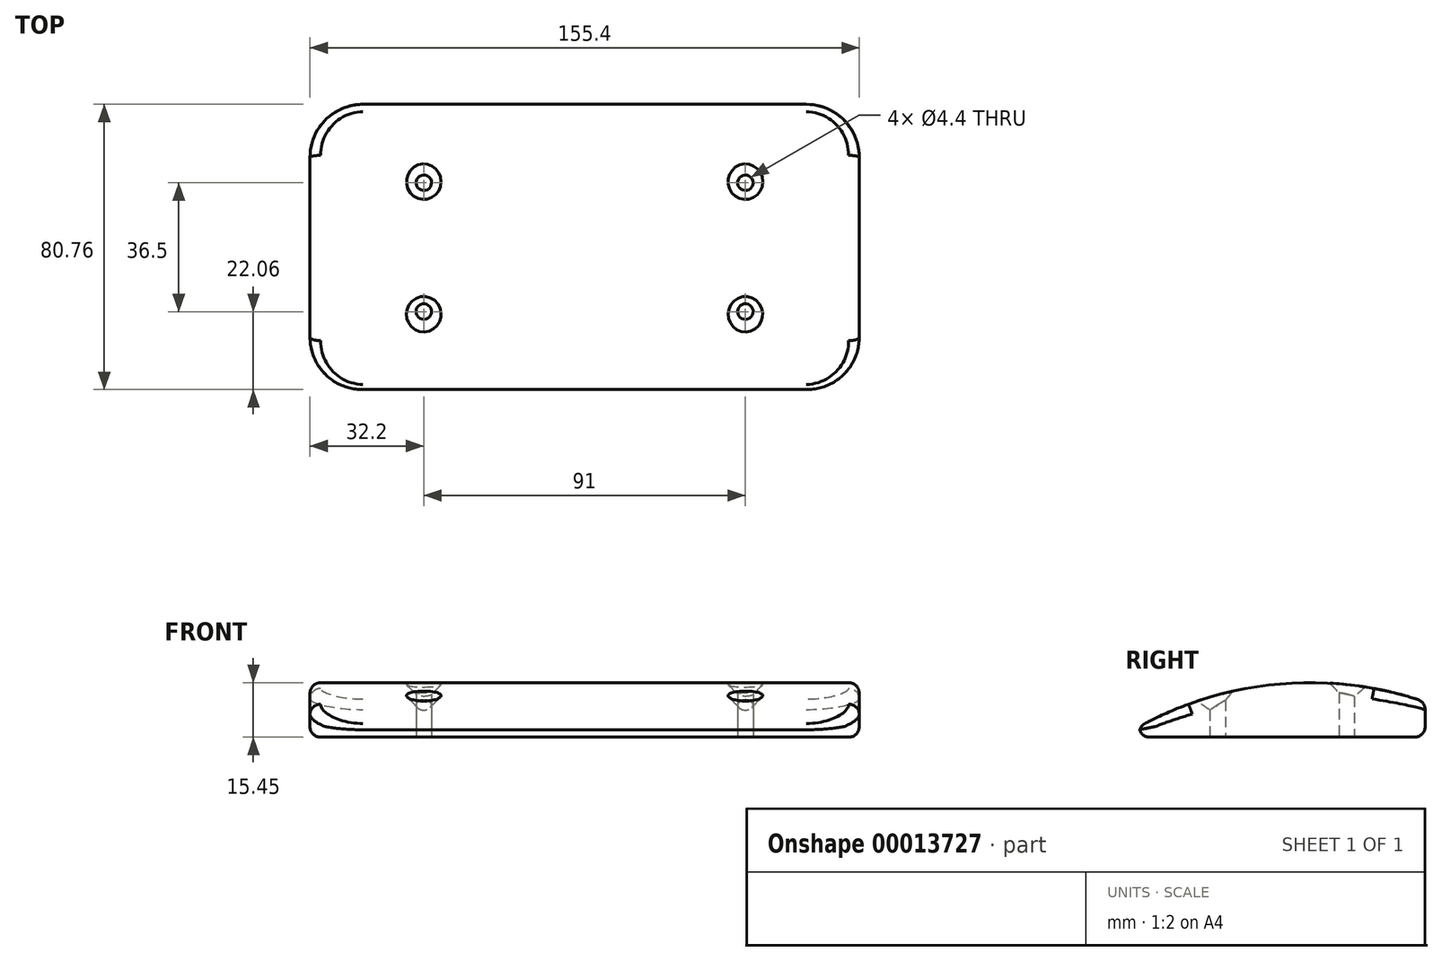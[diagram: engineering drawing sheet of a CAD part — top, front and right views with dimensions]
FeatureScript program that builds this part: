
annotation { "Feature Type Name" : "Feature", "Feature Type Description" : "" }
export const myFeature = defineFeature(function(context is Context, id is Id, definition is map)
    precondition{}
    {
        {
            var Q0;
            Q0=qCreatedBy(makeId("Top.planeOp"),FACE);
            var sketch = newSketch(context, id + "F0", { "sketchPlane" : qUnion([Q0])});
            skLineSegment(sketch, "E0", {"start": v(-45.5, 0) * mm, "end": v(45.5, 0) * mm, "construction": true});
            skLineSegment(sketch, "E1", {"start": v(45.5, 18.25) * mm, "end": v(45.5, -18.25) * mm, "construction": true});
            skLineSegment(sketch, "E2", {"start": v(-45.5, -18.25) * mm, "end": v(-45.5, 18.25) * mm, "construction": true});
            skCircle(sketch, "E3", {"center": v(-45.5, 18.25) * mm, "radius": 2.2 * mm});
            skCircle(sketch, "E4", {"center": v(-45.5, -18.25) * mm, "radius": 2.2 * mm});
            skCircle(sketch, "E5", {"center": v(45.5, -18.25) * mm, "radius": 2.2 * mm});
            skCircle(sketch, "E6", {"center": v(45.5, 18.25) * mm, "radius": 2.2 * mm});
            skLineSegment(sketch, "E7.rect.bottom", {"start": v(-77.7, 40.45) * mm, "end": v(77.7, 40.45) * mm});
            skLineSegment(sketch, "E7.rect.top", {"start": v(-77.7, -40.45) * mm, "end": v(77.7, -40.45) * mm});
            skLineSegment(sketch, "E7.rect.left", {"start": v(-77.7, 40.45) * mm, "end": v(-77.7, -40.45) * mm});
            skLineSegment(sketch, "E7.rect.right", {"start": v(77.7, 40.45) * mm, "end": v(77.7, -40.45) * mm});
            skPoint(sketch, "E7.rect.middle", {"position": v(0, 0) * mm});
            skPoint(sketch, "E8.visualSharp", {"position": v(-77.7, 40.45) * mm});
            skPoint(sketch, "E9.visualSharp", {"position": v(-77.7, -40.45) * mm});
            skPoint(sketch, "E10.visualSharp", {"position": v(77.7, -40.45) * mm});
            skPoint(sketch, "E11.visualSharp", {"position": v(77.7, 40.45) * mm});
            skSolve(sketch);
        }
        {
            var Q0;
            Q0=sQuery(id+"F0.wireOp",EDGE,"E7.rect.left");
            cPlane(context, id + "F1", {"entities" : qUnion([Q0]), "cplaneType" : CPlaneType.LINE_ANGLE, "offset" : 150 * mm, "angle" : 90 * degree, "width" : 150 * mm, "height" : 150 * mm});
        }
        {
            var Q0;
            Q0=qCreatedBy(id+"F1.planeOp",FACE);
            var sketch = newSketch(context, id + "F2", { "sketchPlane" : qUnion([Q0])});
            skLineSegment(sketch, "E12.0", {"start": v(40.45, 0) * mm, "end": v(-40.45, 0) * mm});
            skLineSegment(sketch, "E13", {"start": v(-40.45, 0) * mm, "end": v(-40.45, 3) * mm});
            skLineSegment(sketch, "E14", {"start": v(40.45, 10) * mm, "end": v(40.45, 0) * mm});
            skArc(sketch, "E15", {"start": v(40.45, 10) * mm, "mid": v(-0.74, 15.08) * mm, "end": v(-40.45, 3) * mm});
            skSolve(sketch);
        }
        {
            var Q0;
            Q0=sQuery(id+"F0.wireOp",EDGE,"E7.rect.right");
            cPlane(context, id + "F3", {"entities" : qUnion([Q0]), "cplaneType" : CPlaneType.LINE_ANGLE, "offset" : 150 * mm, "angle" : 90 * degree, "width" : 150 * mm, "height" : 150 * mm});
        }
        {
            var Q0;
            Q0=makeQuery(id+"F2.imprint","IMPRINT",FACE,{"disambiguationData":[TD([[makeQuery(id+"F2.imprint","IMPRINT",EDGE,{"derivedFrom":sQuery(id+"F2.wireOp",EDGE,"E12.0")}),-1.0]])]});
            var Q1;
            Q1=qCreatedBy(id+"F3.planeOp",FACE);
            extrude(context, id + "F4", {"entities" : qUnion([Q0]), "endBound" : BoundingType.UP_TO_SURFACE, "endBoundEntityFace" : qUnion([Q1]), "depth" : 25 * mm});
        }
        {
            var Q0;
            Q0=makeQuery(id+"F0.imprint","IMPRINT",FACE,{"disambiguationData":[TD([[makeQuery(id+"F0.imprint","IMPRINT",EDGE,{"derivedFrom":sQuery(id+"F0.wireOp",EDGE,"E4")}),1.0]])]});
            var Q1;
            Q1=makeQuery(id+"F0.imprint","IMPRINT",FACE,{"disambiguationData":[TD([[makeQuery(id+"F0.imprint","IMPRINT",EDGE,{"derivedFrom":sQuery(id+"F0.wireOp",EDGE,"E3")}),1.0]])]});
            var Q2;
            Q2=makeQuery(id+"F0.imprint","IMPRINT",FACE,{"disambiguationData":[TD([[makeQuery(id+"F0.imprint","IMPRINT",EDGE,{"derivedFrom":sQuery(id+"F0.wireOp",EDGE,"E5")}),1.0]])]});
            var Q3;
            Q3=makeQuery(id+"F0.imprint","IMPRINT",FACE,{"disambiguationData":[TD([[makeQuery(id+"F0.imprint","IMPRINT",EDGE,{"derivedFrom":sQuery(id+"F0.wireOp",EDGE,"E6")}),1.0]])]});
            extrude(context, id + "F5", {"entities" : qUnion([Q0, Q1, Q2, Q3]), "operationType" : NewBodyOperationType.REMOVE, "depth" : 25 * mm});
        }
        {
            var Q0;
            Q0=makeQuery(id+"F5.boolean.opBoolean","INTERSECT",EDGE,{"derivedFrom":[makeQuery(id+"F4.opExtrude","SWEPT_FACE",FACE,{"disambiguationData":[OSD([sQuery(id+"F2.wireOp",EDGE,"E15")])]}),makeQuery(id+"F5.opExtrude","SWEPT_FACE",FACE,{"disambiguationData":[OSD([sQuery(id+"F0.wireOp",EDGE,"E3")])]})]});
            var Q1;
            Q1=makeQuery(id+"F5.boolean.opBoolean","INTERSECT",EDGE,{"derivedFrom":[makeQuery(id+"F4.opExtrude","SWEPT_FACE",FACE,{"disambiguationData":[OSD([sQuery(id+"F2.wireOp",EDGE,"E15")])]}),makeQuery(id+"F5.opExtrude","SWEPT_FACE",FACE,{"disambiguationData":[OSD([sQuery(id+"F0.wireOp",EDGE,"E4")])]})]});
            var Q2;
            Q2=makeQuery(id+"F5.boolean.opBoolean","INTERSECT",EDGE,{"derivedFrom":[makeQuery(id+"F4.opExtrude","SWEPT_FACE",FACE,{"disambiguationData":[OSD([sQuery(id+"F2.wireOp",EDGE,"E15")])]}),makeQuery(id+"F5.opExtrude","SWEPT_FACE",FACE,{"disambiguationData":[OSD([sQuery(id+"F0.wireOp",EDGE,"E5")])]})]});
            var Q3;
            Q3=makeQuery(id+"F5.boolean.opBoolean","INTERSECT",EDGE,{"derivedFrom":[makeQuery(id+"F4.opExtrude","SWEPT_FACE",FACE,{"disambiguationData":[OSD([sQuery(id+"F2.wireOp",EDGE,"E15")])]}),makeQuery(id+"F5.opExtrude","SWEPT_FACE",FACE,{"disambiguationData":[OSD([sQuery(id+"F0.wireOp",EDGE,"E6")])]})]});
            chamfer(context, id + "F6", {"entities" : qUnion([Q0, Q1, Q2, Q3]), "width" : 2.7 * mm, "tangentPropagation" : true});
        }
        {
            var Q0;
            Q0=makeQuery(id+"F4.opExtrude","CAP_EDGE",EDGE,{"disambiguationData":[OSD([sQuery(id+"F2.wireOp",EDGE,"E13")])],"isStart":false});
            var Q1;
            Q1=makeQuery(id+"F4.opExtrude","CAP_EDGE",EDGE,{"disambiguationData":[OSD([sQuery(id+"F2.wireOp",EDGE,"E14")])],"isStart":false});
            var Q2;
            Q2=makeQuery(id+"F4.opExtrude","CAP_EDGE",EDGE,{"disambiguationData":[OSD([sQuery(id+"F2.wireOp",EDGE,"E13")])],"isStart":true});
            var Q3;
            Q3=makeQuery(id+"F4.opExtrude","CAP_EDGE",EDGE,{"disambiguationData":[OSD([sQuery(id+"F2.wireOp",EDGE,"E14")])],"isStart":true});
            fillet(context, id + "F7", {"entities" : qUnion([Q0, Q1, Q2, Q3]), "radius" : 15 * mm, "tangentPropagation" : true, "allowEdgeOverflow" : false});
        }
        {
            var Q0;
            Q0=makeQuery(id+"F4.opExtrude","SWEPT_EDGE",EDGE,{"disambiguationData":[OSD([sQuery(id+"F2.wireOp",EDGE,"E13"),sQuery(id+"F2.wireOp",EDGE,"E15")])]});
            var Q1;
            Q1=makeQuery(id+"F4.opExtrude","SWEPT_EDGE",EDGE,{"disambiguationData":[OSD([sQuery(id+"F2.wireOp",EDGE,"E12.0"),sQuery(id+"F2.wireOp",EDGE,"E13")])]});
            fillet(context, id + "F8", {"entities" : qUnion([Q0, Q1]), "radius" : 3 * mm, "tangentPropagation" : true, "allowEdgeOverflow" : false});
        }
    });
